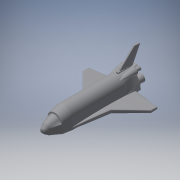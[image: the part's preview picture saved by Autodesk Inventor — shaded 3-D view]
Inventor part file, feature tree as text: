
AUTODESK INVENTOR PART (.ipt)
format: ipt  version: 2018 (Build 220112000, 112)  size: 2,013,696 bytes
history: native  units: in
note: dims shown in document units (in); Inventor stores cm internally (conversion verified against a paired STEP export)
features: sketch x28, plane x15, loft x11, extrude x8, fillet x6, other x3, projected_geometry x3, mirror x2, chamfer x2
ambient origin geometry x8: Origin, YZ Plane, XZ Plane, XY Plane, X Axis, Y Axis, Z Axis, Center Point
bodies: Solid1 (feature_tree)
feature tree (78):
  extrude  "Extrusion1"  TaperAngle=0.0deg  [1 undecoded]
  plane  "Work Plane1"
  plane  "Work Plane2"
  plane  "Work Plane3"
  loft  "Loft1"
  loft  "Loft2"
  fillet  "Fillet1"  Radius=240.6614in
  loft  "Loft4"
  fillet  "Fillet2"  Radius=125.0in
  extrude  "Extrusion2"  TaperAngle=0.0deg  [1 undecoded]
  extrude  "Extrusion3"  Depth=100.0in
  fillet  "Fillet3"  [1 undecoded]
  plane  "Work Plane4"
  mirror  "Mirror1"
  plane  "Work Plane5"
  sketch  "Sketch12"  dims[d36=0.0in d37=90.0deg d38=125.0in]
  loft  "Loft5"
  chamfer  "Chamfer1"  Angle=90.0deg  [1 undecoded]
  chamfer  "Chamfer2"  Angle=90.0deg  [1 undecoded]
  sketch  "Sketch15"  dims[d39=15.0in]
  plane  "Work Plane6"
  plane  "Work Plane7"
  loft  "Loft8"
  mirror  "Mirror2"
  extrude  "Extrusion5"  Depth=125.0in
  extrude  "Extrusion6"  TaperAngle=0.0deg  [1 undecoded]
  plane  "Work Plane8"
  sketch  "Sketch20"  dims[d51=10.0in]
  plane  "Work Plane10"
  loft  "Loft9"
  fillet  "Fillet4"  Radius=84.0in
  extrude  "Extrusion7"  Depth=0.6803in
  fillet  "Fillet5"  Radius=48.0in
  fillet  "Fillet6"  Radius=6500.0in
  sketch  "Sketch23"  dims[d55=0.0in]
  plane  "Work Plane11"
  sketch  "Sketch24"  dims[d56=0.0in]
  loft  "Loft10"
  loft  "Loft11"
  sketch  "Sketch27"  dims[d64=60.0in d70=125.0in]
  plane  "Work Plane12"
  loft  "Loft12"
  loft  "Loft13"
  loft  "Loft14"
  sketch  "Sketch31"  dims[d89=6500.0in d90=7700.0in]
  plane  "Work Plane13"
  sketch  "Sketch32"  dims[d91=10.0in d92=345.0in d93=0.0in]
  sketch  "Sketch33"  dims[d94=10.0in d95=125.0in]
  plane  "Work Plane14"
  extrude  "Extrusion8"  Depth=245.0in
  sketch  "Sketch35"  dims[d98=10.0in d99=0.0in]
  plane  "Work Plane15"
  extrude  "Extrusion9"  Depth=90.0in
  plane  "Work Plane16"
  sketch  "Sketch1"  dims[d5=250.0in d12=0.0in]
  sketch  "Sketch2"  dims[d13=75.0in d15=110.0in]
  other  "Edges1"
  sketch  "Sketch3"  dims[d21=98.0in d24=110.0in d25=240.6614in]
  sketch  "Sketch6"  dims[d26=730.0in d27=0.0in d28=300.0in d29=125.0in]
  sketch  "Sketch7"  dims[d30=250.0in d31=0.0in]
  other  "Edges3"
  sketch  "Sketch8"  dims[d32=125.0in d33=100.0in d34=0.0in d35=90.0deg]
  other  "Edges4"
  sketch  "Sketch17"  dims[d40=20.0in]
  sketch  "Sketch18"  dims[d41=10.0in]
  sketch  "Sketch19"  dims[d50=15.0in]
  projected_geometry  "Projected Loop7"
  sketch  "Sketch21"  dims[d52=75.0in]
  sketch  "Sketch22"  dims[d54=125.0in]
  sketch  "Sketch25"  dims[d57=0.0in d58=0.0in d59=90.0deg d60=0.0in d61=90.0deg]
  sketch  "Sketch26"  dims[d62=10.65in d63=50.0in]
  sketch  "Sketch28"  dims[d71=50.0in d72=0.0in d73=90.0deg]
  sketch  "Sketch29"  dims[d74=0.0in d75=90.0deg d76=40.0in d79=84.0in]
  sketch  "Sketch30"  dims[d80=0.0in d82=0.6803in d83=48.0in d84=0.0in d85=6500.0in]
  sketch  "Sketch34"  dims[d96=200.0in d97=0.0in]
  projected_geometry  "Projected Loop8"
  projected_geometry  "Projected Loop9"
  sketch  "Sketch36"  dims[d100=0.0in d101=245.0in d102=90.0in d105=15.0in d106=0.0618in d107=45.0deg d108=345.0in d109=0.0in d110=90.0deg d111=0.0in d112=90.0deg d113=5.2in d114=0.125in d115=45.0deg d116=5.2in d117=0.125in d118=45.0deg d119=-200.0in d126=100.0in d127=25.0in d133=-205.0in d134=50.0in d135=60.0in d137=0.0in d138=90.0deg d139=0.0in d140=90.0deg d141=160.0in d142=100.0in d143=0.6528in d144=0.0in d145=0.0in d146=9000.0in d147=0.0in d148=15.0in d149=25.0in d150=0.0in d151=30.0in d152=0.0in d153=-20.0in d154=30.0in d155=10.0in d156=1.2162in d157=1.2162in d158=195.0in d160=225.0in d166=30.0in d167=225.0in d168=20.0in d169=30.0in d170=20.0in d171=80.0in d172=0.0in d173=90.0deg d174=0.0in d175=90.0deg d176=7.0in d177=0.1374in d178=200.0in d179=0.0in d180=9.475in d184=150.0in d185=150.0in d186=9.475in d187=40.0in d188=80.0in d189=65.0in d190=60.0in d191=20.0in d192=125.0in d193=0.0in d194=13.0in d195=32.0in d196=55.0in d197=55.0in d198=55.0in d199=80.0in d200=95.0in d201=95.0in d202=40.0in d203=0.0in d204=90.0deg d205=0.0in d206=90.0deg d207=0.0in d208=90.0deg d209=0.0in d210=90.0deg d211=25.0in d212=90.0in d213=8.0in d214=0.0in d215=90.0deg d216=0.0in d217=90.0deg d218=105.0in d219=5.0in d220=5.0in d221=0.0in d222=90.0deg d223=0.0in d224=90.0deg d225=105.0in d226=5.0in d227=5.0in d228=0.0in d229=90.0deg d230=0.0in d231=90.0deg d232=-20.0in d233=90.0deg d234=95.0in d235=0.0in d236=90.0deg d237=105.0in d238=0.0in d239=500.0in]
note: 6 required parameter values undecoded (feature->parameter linkage not recoverable at this tier; creation-order binding heuristic only, values carry confidence <= 0.55)
